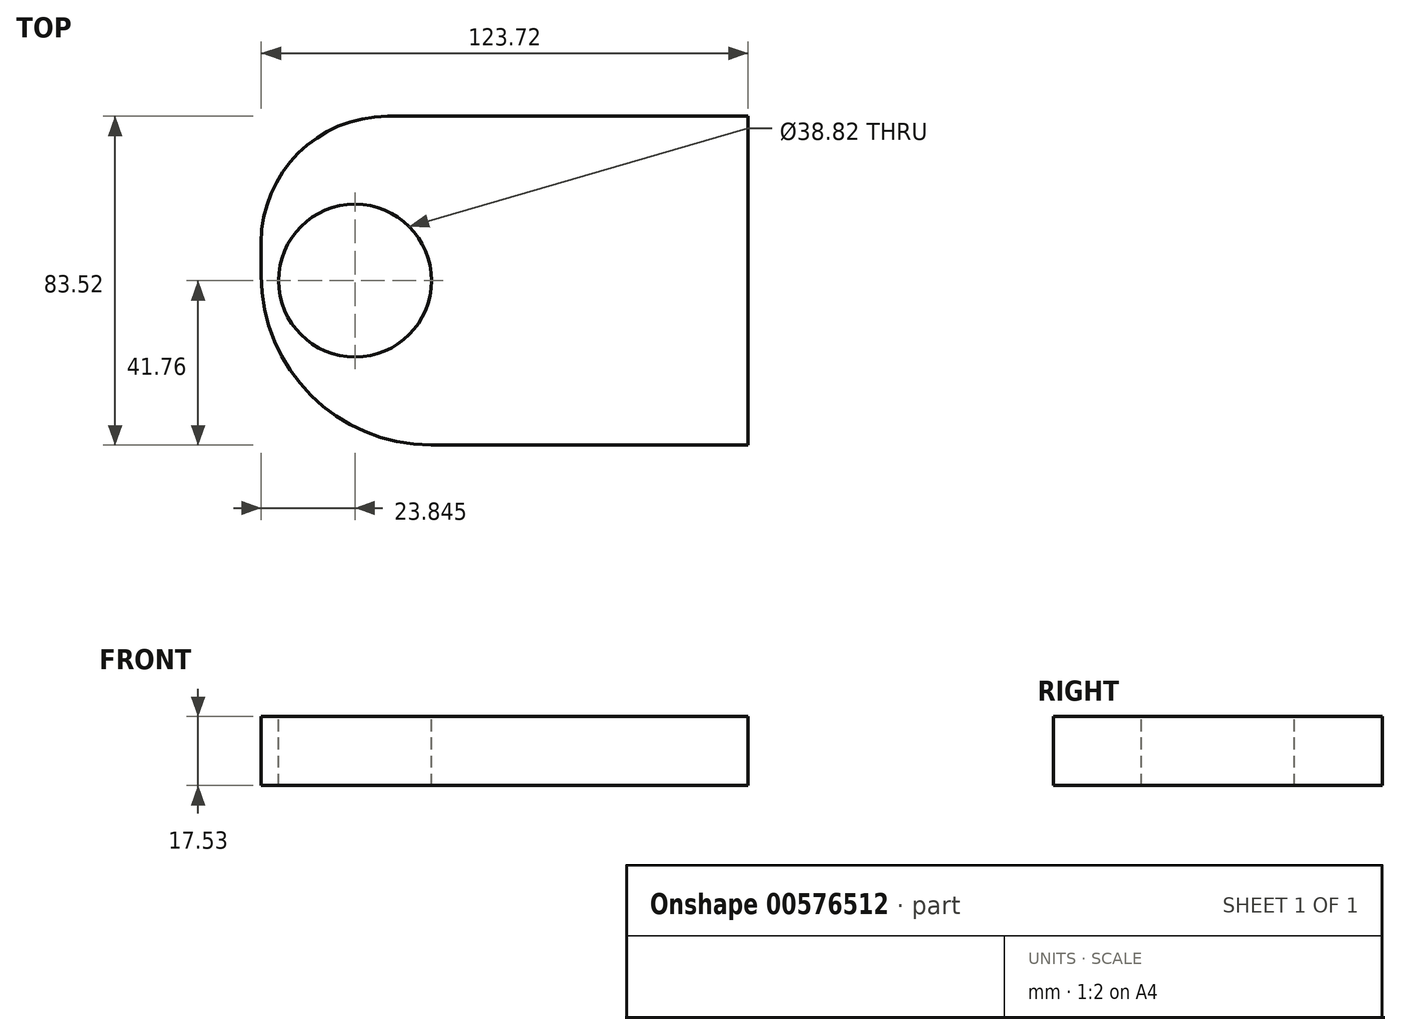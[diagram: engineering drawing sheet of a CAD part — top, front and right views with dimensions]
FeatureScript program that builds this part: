
annotation { "Feature Type Name" : "Feature", "Feature Type Description" : "" }
export const myFeature = defineFeature(function(context is Context, id is Id, definition is map)
    precondition{}
    {
        {
            var Q0;
            Q0=qCreatedBy(makeId("Top.planeOp"),FACE);
            var sketch = newSketch(context, id + "F0", { "sketchPlane" : qUnion([Q0])});
            skLineSegment(sketch, "E0.bottom", {"start": v(61.86, 41.76) * mm, "end": v(-29.77, 41.76) * mm});
            skLineSegment(sketch, "E0.top", {"start": v(61.86, -41.76) * mm, "end": v(-18.73, -41.76) * mm});
            skLineSegment(sketch, "E0.left", {"start": v(61.86, 41.76) * mm, "end": v(61.86, -41.76) * mm});
            skLineSegment(sketch, "E0.right", {"start": v(-61.86, 9.68) * mm, "end": v(-61.86, 1.37) * mm});
            skPoint(sketch, "E0.middle", {"position": v(0, 0) * mm});
            skPoint(sketch, "E1.visualSharp", {"position": v(-61.86, 41.76) * mm});
            skArc(sketch, "E1.filletArc", {"start": v(-29.77, 41.76) * mm, "mid": v(-52.46, 32.37) * mm, "end": v(-61.86, 9.68) * mm});
            skPoint(sketch, "E2.visualSharp", {"position": v(-61.86, -41.76) * mm});
            skArc(sketch, "E2.filletArc", {"start": v(-61.86, 1.37) * mm, "mid": v(-49.22, -29.13) * mm, "end": v(-18.73, -41.76) * mm});
            skSolve(sketch);
        }
        {
            var Q0;
            Q0=makeQuery(id+"F0.imprint","IMPRINT",FACE,{"disambiguationData":[TD([[makeQuery(id+"F0.imprint","IMPRINT",EDGE,{"derivedFrom":sQuery(id+"F0.wireOp",EDGE,"E0.bottom")}),1.0]])]});
            extrude(context, id + "F1", {"entities" : qUnion([Q0]), "depth" : 17.53 * mm, "offsetDistance" : 25.4 * mm});
        }
        {
            var Q0;
            Q0=makeQuery(id+"F1.opExtrude","CAP_FACE",FACE,{"disambiguationData":[OSD([sQuery(id+"F0.wireOp",EDGE,"E0.bottom"),sQuery(id+"F0.wireOp",EDGE,"E0.top"),sQuery(id+"F0.wireOp",EDGE,"E0.left"),sQuery(id+"F0.wireOp",EDGE,"E0.right")])],"isStart":false});
            var sketch = newSketch(context, id + "F2", { "sketchPlane" : qUnion([Q0])});
            skCircle(sketch, "E3", {"center": v(-38.02, 0) * mm, "radius": 19.4 * mm});
            skSolve(sketch);
        }
        {
            var Q0;
            Q0=makeQuery(id+"F2.imprint","IMPRINT",FACE,{"disambiguationData":[TD([[makeQuery(id+"F2.imprint","IMPRINT",EDGE,{"derivedFrom":sQuery(id+"F2.wireOp",EDGE,"E3")}),1.0]])]});
            extrude(context, id + "F3", {"entities" : qUnion([Q0]), "operationType" : NewBodyOperationType.REMOVE, "endBound" : BoundingType.THROUGH_ALL, "oppositeDirection" : true, "depth" : 25.4 * mm, "offsetDistance" : 25.4 * mm});
        }
    });
